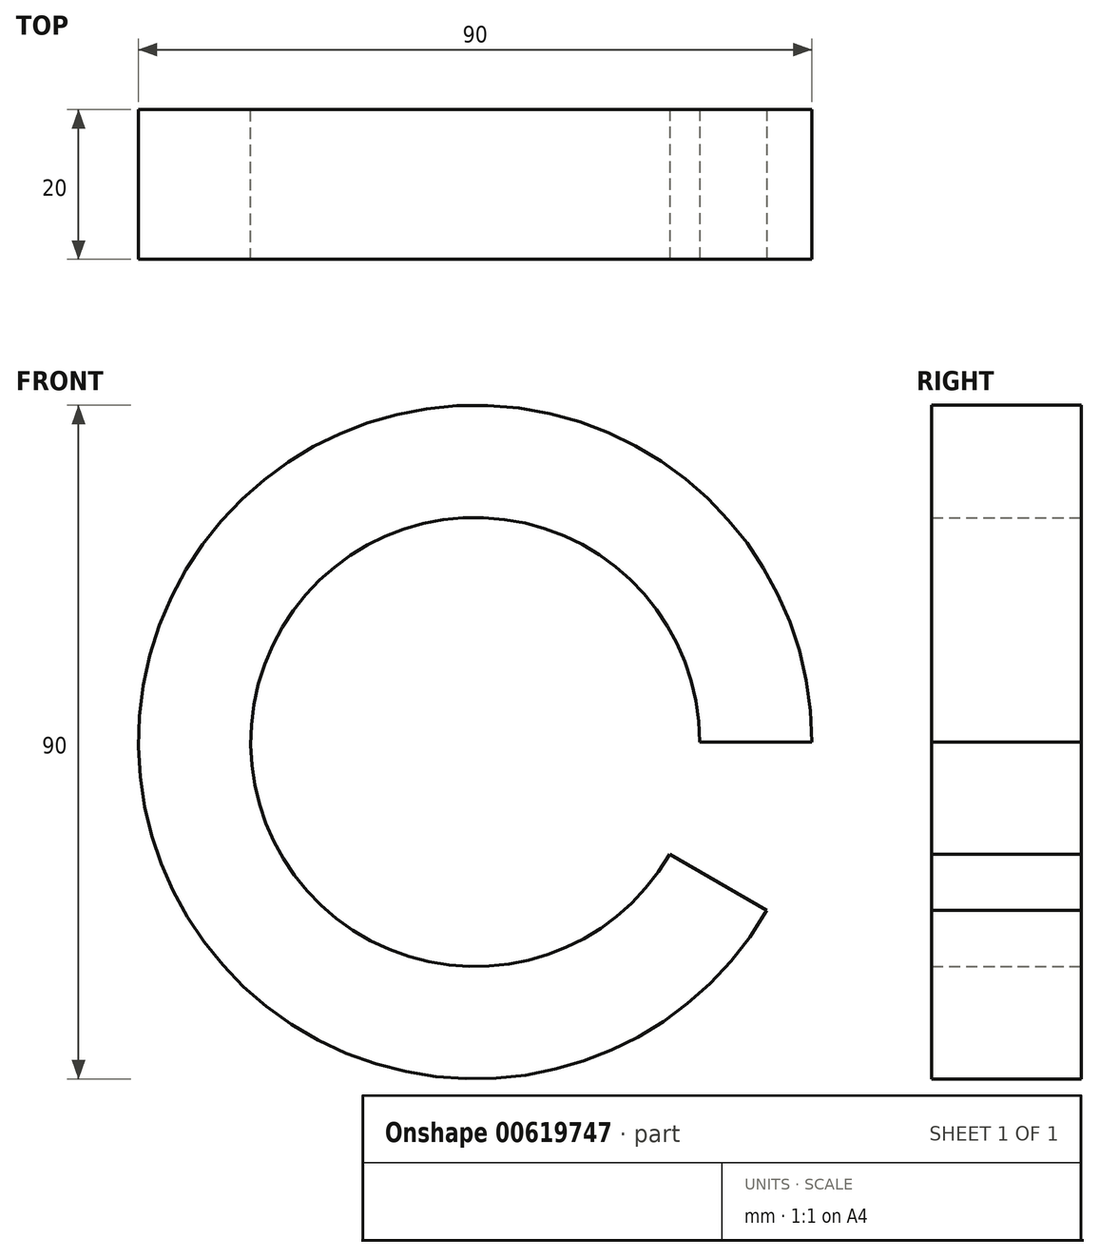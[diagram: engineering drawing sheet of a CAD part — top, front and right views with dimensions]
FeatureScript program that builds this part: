
annotation { "Feature Type Name" : "Feature", "Feature Type Description" : "" }
export const myFeature = defineFeature(function(context is Context, id is Id, definition is map)
    precondition{}
    {
        {
            var Q0;
            Q0=qCreatedBy(makeId("Top.planeOp"),FACE);
            var sketch = newSketch(context, id + "F0", { "sketchPlane" : qUnion([Q0])});
            skLineSegment(sketch, "E0.bottom", {"start": v(30, 0) * mm, "end": v(45, 0) * mm});
            skLineSegment(sketch, "E0.top", {"start": v(30, -20) * mm, "end": v(45, -20) * mm});
            skLineSegment(sketch, "E0.left", {"start": v(30, 0) * mm, "end": v(30, -20) * mm});
            skLineSegment(sketch, "E0.right", {"start": v(45, 0) * mm, "end": v(45, -20) * mm});
            skLineSegment(sketch, "E1", {"start": v(0, 0) * mm, "end": v(0, -29.04) * mm, "construction": true});
            skSolve(sketch);
        }
        {
            var Q0;
            Q0=makeQuery(id+"F0.imprint","IMPRINT",FACE,{"disambiguationData":[TD([[makeQuery(id+"F0.imprint","IMPRINT",EDGE,{"derivedFrom":sQuery(id+"F0.wireOp",EDGE,"E0.bottom")}),-1.0]])]});
            var Q1;
            Q1=sQuery(id+"F0.wireOp",EDGE,"E1");
            revolve(context, id + "F1", {"entities" : qUnion([Q0]), "axis" : qUnion([Q1]), "revolveType" : RevolveType.ONE_DIRECTION, "angle" : 330 * degree});
        }
    });
